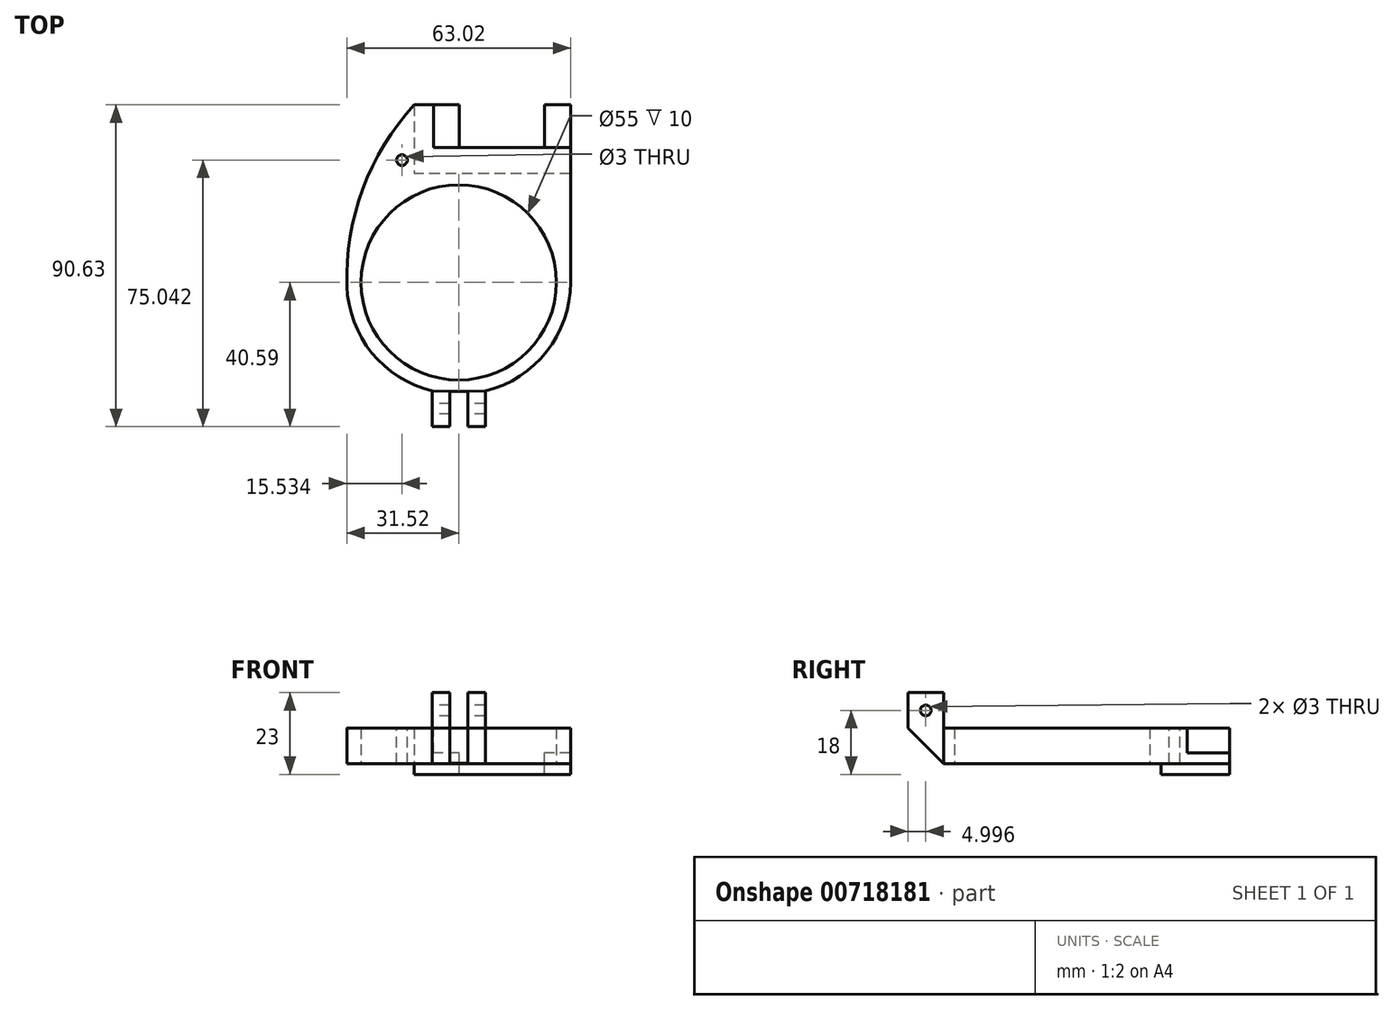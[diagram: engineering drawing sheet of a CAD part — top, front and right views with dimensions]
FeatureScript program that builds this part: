
annotation { "Feature Type Name" : "Feature", "Feature Type Description" : "" }
export const myFeature = defineFeature(function(context is Context, id is Id, definition is map)
    precondition{}
    {
        {
            var Q0;
            Q0=qCreatedBy(makeId("Top.planeOp"),FACE);
            var sketch = newSketch(context, id + "F0", { "sketchPlane" : qUnion([Q0])});
            skCircle(sketch, "E0", {"center": v(0, 0) * mm, "radius": 27.5 * mm});
            skArc(sketch, "E1", {"start": v(-31.48, -1.05) * mm, "mid": v(-24.46, -19.85) * mm, "end": v(-7.5, -30.6) * mm});
            skLineSegment(sketch, "E2.top", {"start": v(-7.5, -40.6) * mm, "end": v(-2.5, -40.6) * mm});
            skLineSegment(sketch, "E2.left", {"start": v(-7.5, -30.6) * mm, "end": v(-7.5, -40.6) * mm});
            skLineSegment(sketch, "E2.right", {"start": v(7.5, -30.6) * mm, "end": v(7.5, -40.6) * mm});
            skLineSegment(sketch, "E3.top", {"start": v(31.5, 50.04) * mm, "end": v(-12.5, 50.04) * mm});
            skLineSegment(sketch, "E3.left", {"start": v(31.5, 0) * mm, "end": v(31.5, 50.04) * mm});
            skArc(sketch, "E4.trimOffspring", {"start": v(7.5, -30.6) * mm, "mid": v(24.78, -19.44) * mm, "end": v(31.5, 0) * mm});
            skLineSegment(sketch, "E5.bottom", {"start": v(-2.5, -30.71) * mm, "end": v(2.5, -30.71) * mm});
            skLineSegment(sketch, "E5.left", {"start": v(-2.5, -30.71) * mm, "end": v(-2.5, -40.6) * mm});
            skLineSegment(sketch, "E5.right", {"start": v(2.5, -30.71) * mm, "end": v(2.5, -40.6) * mm});
            skLineSegment(sketch, "E6.trimOffspring", {"start": v(2.5, -40.6) * mm, "end": v(7.5, -40.6) * mm});
            skLineSegment(sketch, "E7", {"start": v(2.5, -30.71) * mm, "end": v(7.5, -30.6) * mm});
            skLineSegment(sketch, "E8", {"start": v(-2.5, -30.71) * mm, "end": v(-7.5, -30.6) * mm});
            skArc(sketch, "E9", {"start": v(-31.48, -1.05) * mm, "mid": v(-27.03, 26.36) * mm, "end": v(-12.5, 50.04) * mm});
            skSolve(sketch);
        }
        {
            var Q0;
            Q0=makeQuery(id+"F0.imprint","IMPRINT",FACE,{"disambiguationData":[TD([[makeQuery(id+"F0.imprint","IMPRINT",EDGE,{"derivedFrom":sQuery(id+"F0.wireOp",EDGE,"E0")}),-1.0]])]});
            extrude(context, id + "F1", {"entities" : qUnion([Q0]), "depth" : 10 * mm, "offsetDistance" : 25 * mm});
        }
        {
            var Q0;
            Q0=makeQuery(id+"F0.imprint","IMPRINT",FACE,{"disambiguationData":[TD([[makeQuery(id+"F0.imprint","IMPRINT",EDGE,{"derivedFrom":sQuery(id+"F0.wireOp",EDGE,"E2.right")}),-1.0]])]});
            var Q1;
            Q1=makeQuery(id+"F0.imprint","IMPRINT",FACE,{"disambiguationData":[TD([[makeQuery(id+"F0.imprint","IMPRINT",EDGE,{"derivedFrom":sQuery(id+"F0.wireOp",EDGE,"E2.top")}),1.0]])]});
            extrude(context, id + "F2", {"entities" : qUnion([Q0, Q1]), "operationType" : NewBodyOperationType.ADD, "depth" : 20 * mm, "offsetDistance" : 25 * mm});
        }
        {
            var Q0;
            Q0=makeQuery(id+"F2.opExtrude","SWEPT_FACE",FACE,{"disambiguationData":[OSD([sQuery(id+"F0.wireOp",EDGE,"E2.left")])]});
            var sketch = newSketch(context, id + "F3", { "sketchPlane" : qUnion([Q0])});
            skPoint(sketch, "E10.endSnap0", {"position": v(40.6, 10) * mm});
            skLineSegment(sketch, "E11", {"start": v(30.6, 0) * mm, "end": v(40.6, 10) * mm});
            skSolve(sketch);
        }
        {
            var Q0;
            {var subQ0=sQuery(id+"F3.wireOp",EDGE,"E11");Q0=makeQuery(id+"F3.imprint","IMPRINT",FACE,{"disambiguationData":[TD([[makeQuery(id+"F3.imprint","IMPRINT",EDGE,{"derivedFrom":subQ0}),-1.0]])]});}
            extrude(context, id + "F4", {"entities" : qUnion([Q0]), "operationType" : NewBodyOperationType.REMOVE, "oppositeDirection" : true, "depth" : 25 * mm, "offsetDistance" : 25 * mm});
        }
        {
            var Q0;
            Q0=makeQuery(id+"F1.opExtrude","CAP_FACE",FACE,{"disambiguationData":[OSD([sQuery(id+"F0.wireOp",EDGE,"E0"),sQuery(id+"F0.wireOp",EDGE,"E1"),sQuery(id+"F0.wireOp",EDGE,"E3.top"),sQuery(id+"F0.wireOp",EDGE,"E3.left"),sQuery(id+"F0.wireOp",EDGE,"e5b498fd-03dc-4419-9677-880219975f82"),sQuery(id+"F0.wireOp",EDGE,"E4.trimOffspring"),sQuery(id+"F0.wireOp",EDGE,"E5.bottom"),sQuery(id+"F0.wireOp",EDGE,"E7"),sQuery(id+"F0.wireOp",EDGE,"E8")])],"isStart":false});
            var sketch = newSketch(context, id + "F5", { "sketchPlane" : qUnion([Q0])});
            skLineSegment(sketch, "E12.bottom", {"start": v(-7.12, 50.04) * mm, "end": v(32.88, 50.04) * mm});
            skLineSegment(sketch, "E12.top", {"start": v(-7.12, 38.04) * mm, "end": v(32.88, 38.04) * mm});
            skLineSegment(sketch, "E12.left", {"start": v(-7.12, 50.04) * mm, "end": v(-7.12, 38.04) * mm});
            skLineSegment(sketch, "E12.right", {"start": v(32.88, 50.04) * mm, "end": v(32.88, 38.04) * mm});
            skSolve(sketch);
        }
        {
            var Q0;
            Q0=makeQuery(id+"F5.imprint","IMPRINT",FACE,{"disambiguationData":[TD([[makeQuery(id+"F5.imprint","IMPRINT",EDGE,{"derivedFrom":sQuery(id+"F5.wireOp",EDGE,"E12.bottom")}),1.0]])]});
            extrude(context, id + "F6", {"entities" : qUnion([Q0]), "operationType" : NewBodyOperationType.REMOVE, "oppositeDirection" : true, "depth" : 7 * mm, "offsetDistance" : 25 * mm});
        }
        {
            var Q0;
            Q0=makeQuery(id+"F6.boolean.opBoolean","COPY",FACE,{"derivedFrom":makeQuery(id+"F6.opExtrude","CAP_FACE",FACE,{"disambiguationData":[OSD([sQuery(id+"F5.wireOp",EDGE,"E12.bottom"),sQuery(id+"F5.wireOp",EDGE,"E12.top"),sQuery(id+"F5.wireOp",EDGE,"E12.left"),sQuery(id+"F5.wireOp",EDGE,"E12.right")])],"isStart":false})});
            var sketch = newSketch(context, id + "F7", { "sketchPlane" : qUnion([Q0])});
            skLineSegment(sketch, "E13.bottom", {"start": v(0.18, 50.04) * mm, "end": v(24.18, 50.04) * mm});
            skLineSegment(sketch, "E13.top", {"start": v(0.18, 38.04) * mm, "end": v(24.18, 38.04) * mm});
            skLineSegment(sketch, "E13.left", {"start": v(0.18, 50.04) * mm, "end": v(0.18, 38.04) * mm});
            skLineSegment(sketch, "E13.right", {"start": v(24.18, 50.04) * mm, "end": v(24.18, 38.04) * mm});
            skSolve(sketch);
        }
        {
            var Q0;
            Q0=makeQuery(id+"F0.imprint","IMPRINT",FACE,{"disambiguationData":[TD([[makeQuery(id+"F0.imprint","IMPRINT",EDGE,{"derivedFrom":sQuery(id+"F0.wireOp",EDGE,"E0")}),-1.0]])]});
            var sketch = newSketch(context, id + "F8", { "sketchPlane" : qUnion([Q0])});
            skLineSegment(sketch, "E14.bottom", {"start": v(31.47, 49.97) * mm, "end": v(-12.6, 49.97) * mm});
            skLineSegment(sketch, "E14.top", {"start": v(31.47, 30.61) * mm, "end": v(-12.6, 30.61) * mm});
            skLineSegment(sketch, "E14.left", {"start": v(31.47, 49.97) * mm, "end": v(31.47, 30.61) * mm});
            skLineSegment(sketch, "E14.right", {"start": v(-12.6, 49.97) * mm, "end": v(-12.6, 30.61) * mm});
            skSolve(sketch);
        }
        {
            var Q0;
            Q0 = qSketchRegion(id + "F8", true);
            extrude(context, id + "F9", {"entities" : qUnion([Q0]), "operationType" : NewBodyOperationType.ADD, "oppositeDirection" : true, "depth" : 3 * mm, "offsetDistance" : 25 * mm});
        }
        {
            var Q0;
            Q0=makeQuery(id+"F7.imprint","IMPRINT",FACE,{"disambiguationData":[TD([[makeQuery(id+"F7.imprint","IMPRINT",EDGE,{"derivedFrom":sQuery(id+"F7.wireOp",EDGE,"E13.bottom")}),1.0]])]});
            extrude(context, id + "F10", {"entities" : qUnion([Q0]), "operationType" : NewBodyOperationType.REMOVE, "oppositeDirection" : true, "depth" : 25 * mm, "offsetDistance" : 25 * mm});
        }
        {
            var Q0;
            Q0=makeQuery(id+"F1.opExtrude","CAP_FACE",FACE,{"disambiguationData":[OSD([sQuery(id+"F0.wireOp",EDGE,"E0"),sQuery(id+"F0.wireOp",EDGE,"E1"),sQuery(id+"F0.wireOp",EDGE,"E3.top"),sQuery(id+"F0.wireOp",EDGE,"E3.left"),sQuery(id+"F0.wireOp",EDGE,"E4.trimOffspring"),sQuery(id+"F0.wireOp",EDGE,"E5.bottom"),sQuery(id+"F0.wireOp",EDGE,"E7"),sQuery(id+"F0.wireOp",EDGE,"E8"),sQuery(id+"F0.wireOp",EDGE,"E9")])],"isStart":false});
            var sketch = newSketch(context, id + "F11", { "sketchPlane" : qUnion([Q0])});
            skCircle(sketch, "E15", {"center": v(-15.99, 34.45) * mm, "radius": 1.5 * mm});
            skSolve(sketch);
        }
        {
            var Q0;
            Q0=makeQuery(id+"F11.imprint","IMPRINT",FACE,{"disambiguationData":[TD([[makeQuery(id+"F11.imprint","IMPRINT",EDGE,{"derivedFrom":sQuery(id+"F11.wireOp",EDGE,"E15")}),1.0]])]});
            extrude(context, id + "F12", {"entities" : qUnion([Q0]), "operationType" : NewBodyOperationType.REMOVE, "oppositeDirection" : true, "depth" : 25 * mm, "offsetDistance" : 25 * mm});
        }
        {
            var Q0;
            Q0=makeQuery(id+"F2.opExtrude","SWEPT_FACE",FACE,{"disambiguationData":[OSD([sQuery(id+"F0.wireOp",EDGE,"E2.left")])]});
            var sketch = newSketch(context, id + "F13", { "sketchPlane" : qUnion([Q0])});
            skCircle(sketch, "E16", {"center": v(35.6, 15) * mm, "radius": 1.5 * mm});
            skSolve(sketch);
        }
        {
            var Q0;
            Q0=makeQuery(id+"F13.imprint","IMPRINT",FACE,{"disambiguationData":[TD([[makeQuery(id+"F13.imprint","IMPRINT",EDGE,{"derivedFrom":sQuery(id+"F13.wireOp",EDGE,"E16")}),1.0]])]});
            extrude(context, id + "F14", {"entities" : qUnion([Q0]), "operationType" : NewBodyOperationType.REMOVE, "oppositeDirection" : true, "depth" : 25 * mm, "offsetDistance" : 25 * mm});
        }
    });
